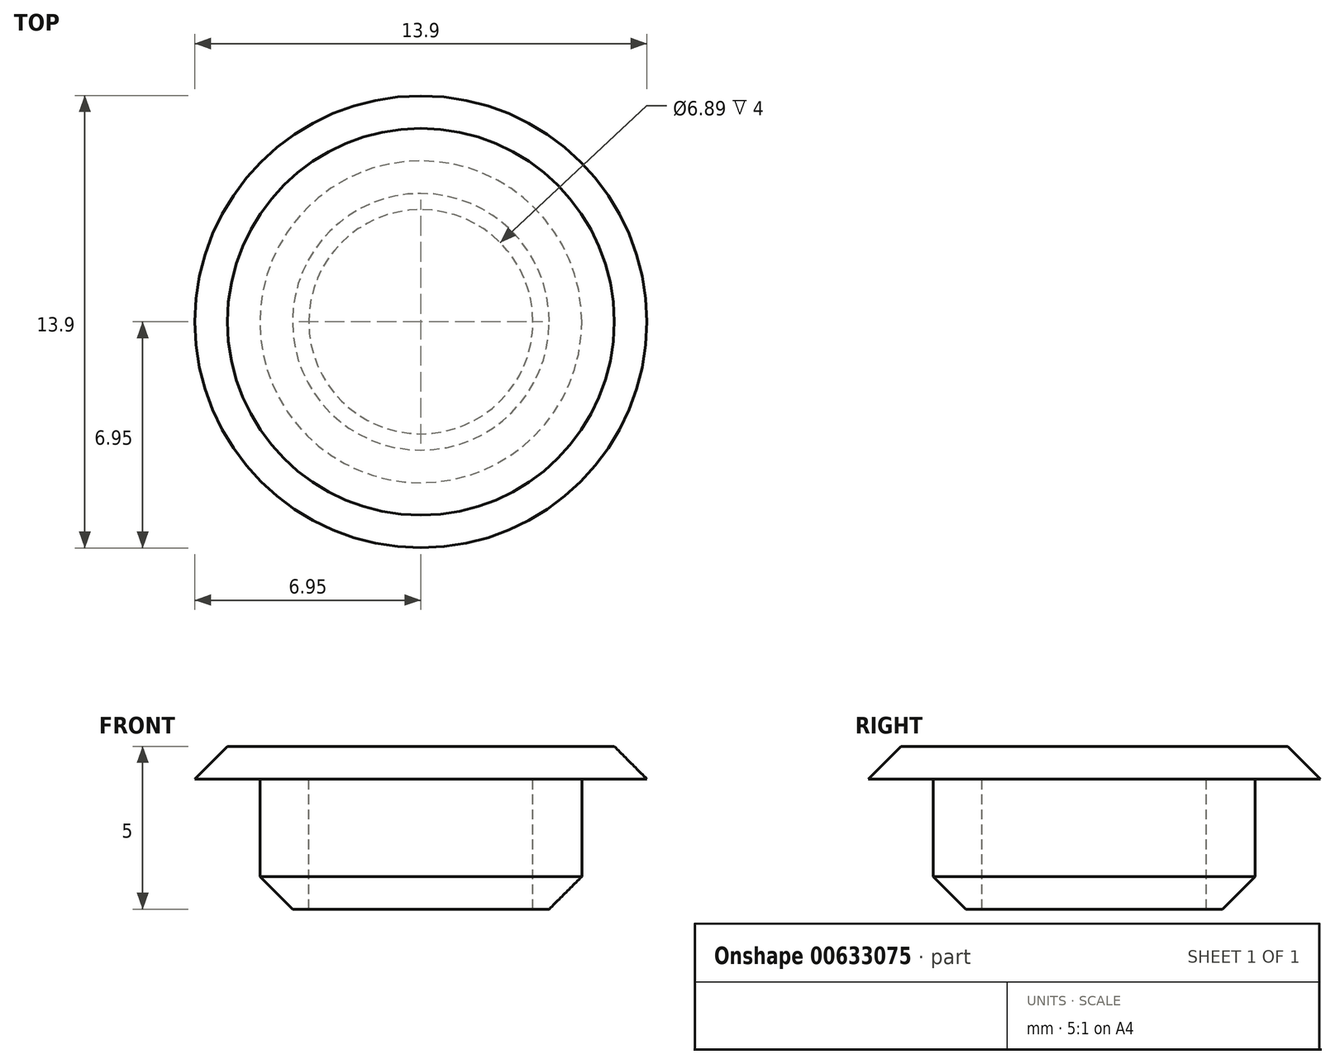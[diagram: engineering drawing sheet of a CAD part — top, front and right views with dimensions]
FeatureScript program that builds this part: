
annotation { "Feature Type Name" : "Feature", "Feature Type Description" : "" }
export const myFeature = defineFeature(function(context is Context, id is Id, definition is map)
    precondition{}
    {
        {
            var Q0;
            Q0=qCreatedBy(makeId("Top.planeOp"),FACE);
            var sketch = newSketch(context, id + "F0", { "sketchPlane" : qUnion([Q0])});
            skCircle(sketch, "E0", {"center": v(0, 0) * mm, "radius": 4.95 * mm});
            skCircle(sketch, "E1.0", {"center": v(0, 0) * mm, "radius": 6.95 * mm});
            skCircle(sketch, "E2.0", {"center": v(0, 0) * mm, "radius": 3.45 * mm});
            skSolve(sketch);
        }
        {
            var Q0;
            Q0=makeQuery(id+"F0.imprint","IMPRINT",FACE,{"disambiguationData":[TD([[makeQuery(id+"F0.imprint","IMPRINT",EDGE,{"derivedFrom":sQuery(id+"F0.wireOp",EDGE,"E0")}),1.0]])]});
            extrude(context, id + "F1", {"entities" : qUnion([Q0]), "oppositeDirection" : true, "depth" : 4 * mm, "offsetDistance" : 25 * mm});
        }
        {
            var Q0;
            Q0 = qSketchRegion(id + "F0", true);
            var Q1;
            Q1=makeQuery(id+"F1.opExtrude","CAP_FACE",FACE,{"disambiguationData":[OSD([sQuery(id+"F0.wireOp",EDGE,"E0")])],"isStart":true});
            var Q2;
            Q2=makeQuery(id+"F0.imprint","IMPRINT",FACE,{"disambiguationData":[TD([[makeQuery(id+"F0.imprint","IMPRINT",EDGE,{"derivedFrom":sQuery(id+"F0.wireOp",EDGE,"E2.0")}),1.0]])]});
            extrude(context, id + "F2", {"entities" : qUnion([Q0, Q1, Q2]), "operationType" : NewBodyOperationType.ADD, "depth" : 1 * mm, "offsetDistance" : 25 * mm});
        }
        {
            var Q0;
            Q0=makeQuery(id+"F2.opExtrude","CAP_EDGE",EDGE,{"disambiguationData":[OSD([sQuery(id+"F0.wireOp",EDGE,"E1.0")])],"isStart":false});
            chamfer(context, id + "F3", {"entities" : qUnion([Q0]), "width" : 1 * mm, "tangentPropagation" : true});
        }
        {
            var Q0;
            Q0=makeQuery(id+"F1.opExtrude","CAP_EDGE",EDGE,{"disambiguationData":[OSD([sQuery(id+"F0.wireOp",EDGE,"E0")])],"isStart":false});
            chamfer(context, id + "F4", {"entities" : qUnion([Q0]), "chamferType" : ChamferType.TWO_OFFSETS, "width1" : 1 * mm, "oppositeDirection" : false, "width2" : 1 * mm, "tangentPropagation" : true});
        }
    });
